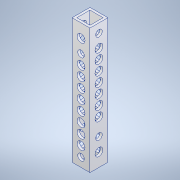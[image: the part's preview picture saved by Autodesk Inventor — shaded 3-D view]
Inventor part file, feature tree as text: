
AUTODESK INVENTOR PART (.ipt)
format: ipt  version: 2020.3 (Build 243373000, 373)  size: 224,256 bytes
history: native  units: mm
features: sketch x6, hole x5, other x1, extrude x1
ambient origin geometry x8: Origin, YZ Plane, XZ Plane, XY Plane, X Axis, Y Axis, Z Axis, Center Point
bodies: Body1 (feature_tree)
feature tree (13):
  other  "ソリッド1"
  extrude  "押し出し1"  Depth=9.0mm
  hole  "穴1"  [1 undecoded]
  hole  "穴2"  [1 undecoded]
  hole  "穴3"  [1 undecoded]
  hole  "穴4"  [1 undecoded]
  hole  "穴5"  [1 undecoded]
  sketch  "スケッチ1"
  sketch  "スケッチ2"
  sketch  "スケッチ3"
  sketch  "スケッチ4"
  sketch  "スケッチ5"
  sketch  "スケッチ7"
note: 5 required parameter values undecoded (feature->parameter linkage not recoverable at this tier; creation-order binding heuristic only, values carry confidence <= 0.55)
